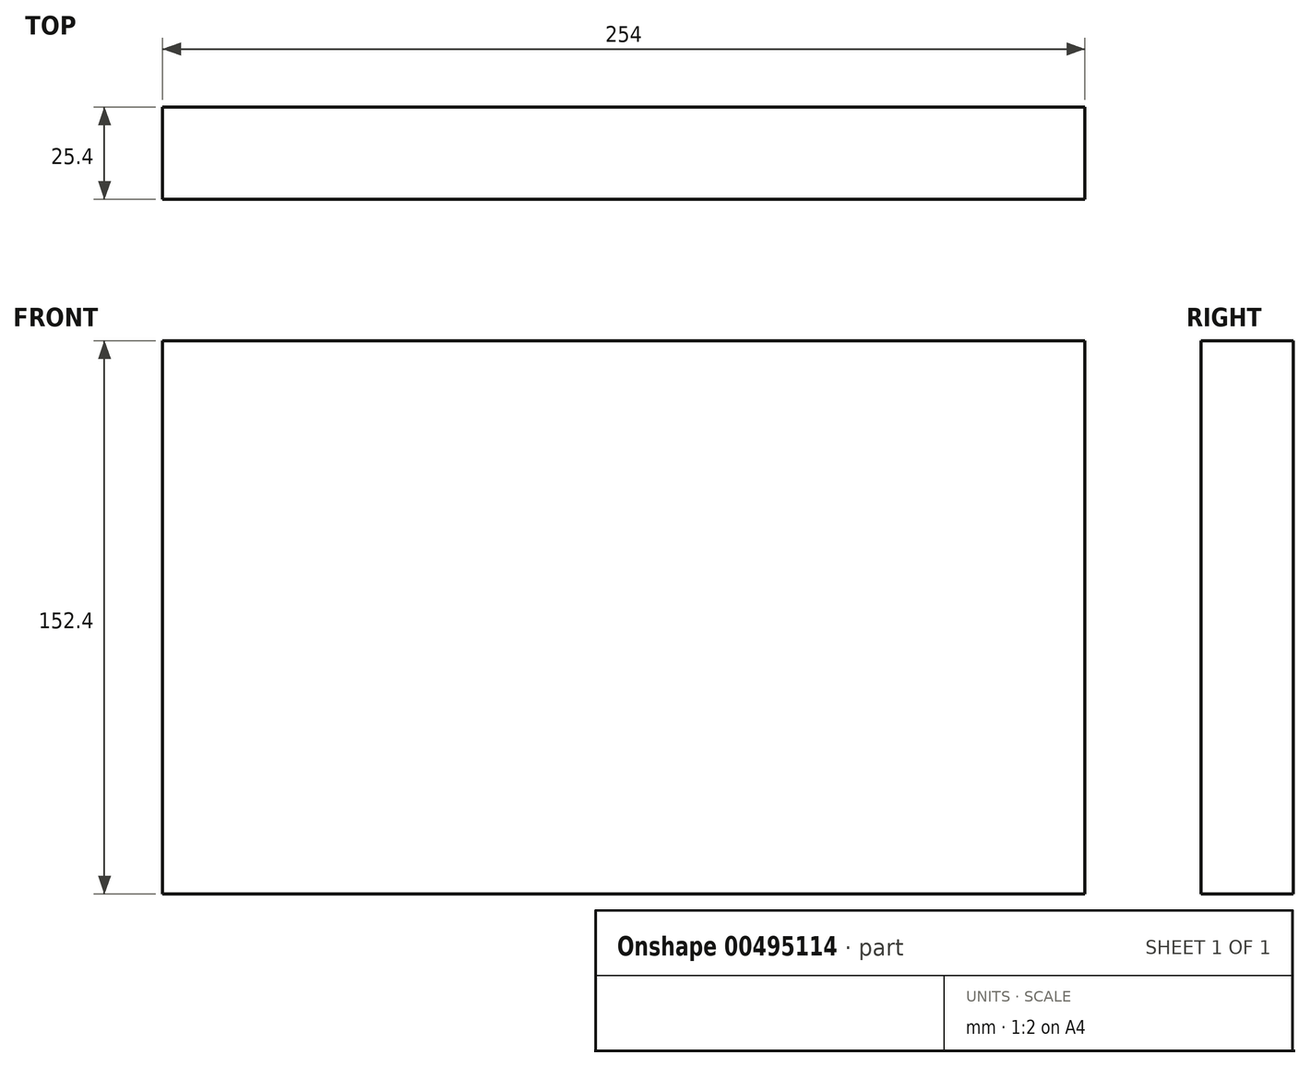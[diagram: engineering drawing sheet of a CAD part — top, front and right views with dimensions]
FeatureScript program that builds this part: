
annotation { "Feature Type Name" : "Feature", "Feature Type Description" : "" }
export const myFeature = defineFeature(function(context is Context, id is Id, definition is map)
    precondition{}
    {
        {
            var Q0;
            Q0=qCreatedBy(makeId("Front.planeOp"),FACE);
            var sketch = newSketch(context, id + "F0", { "sketchPlane" : qUnion([Q0])});
            skLineSegment(sketch, "E0.bottom", {"start": v(0, 0) * mm, "end": v(-254, 0) * mm});
            skLineSegment(sketch, "E0.top", {"start": v(0, 152.4) * mm, "end": v(-254, 152.4) * mm});
            skLineSegment(sketch, "E0.left", {"start": v(0, 0) * mm, "end": v(0, 152.4) * mm});
            skLineSegment(sketch, "E0.right", {"start": v(-254, 0) * mm, "end": v(-254, 152.4) * mm});
            skSolve(sketch);
        }
        {
            var Q0;
            Q0=makeQuery(id+"F0.imprint","IMPRINT",FACE,{"disambiguationData":[TD([[makeQuery(id+"F0.imprint","IMPRINT",EDGE,{"derivedFrom":sQuery(id+"F0.wireOp",EDGE,"E0.bottom")}),-1.0]])]});
            extrude(context, id + "F1", {"entities" : qUnion([Q0]), "depth" : 25.4 * mm});
        }
    });
